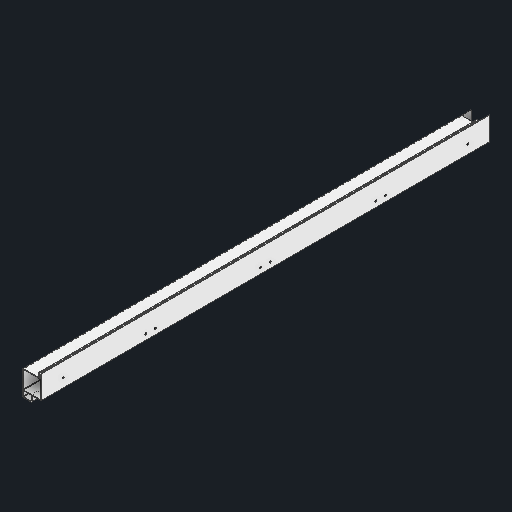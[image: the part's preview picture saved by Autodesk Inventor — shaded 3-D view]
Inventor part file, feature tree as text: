
AUTODESK INVENTOR PART (.ipt)
format: ipt  version: 2024.2 (Build 282272000, 272)  size: 155,136 bytes
history: native  units: in
note: dims shown in document units (in); Inventor stores cm internally (conversion verified against a paired STEP export)
features: fillet x1
ambient origin geometry x8: Origin, YZ Plane, XZ Plane, XY Plane, X Axis, Y Axis, Z Axis, Center Point
bodies: Solid1 (feature_tree)
feature tree (1):
  fillet  "Fillet6"  [1 undecoded]
note: 1 required parameter value undecoded (feature->parameter linkage not recoverable at this tier; creation-order binding heuristic only, values carry confidence <= 0.55)
